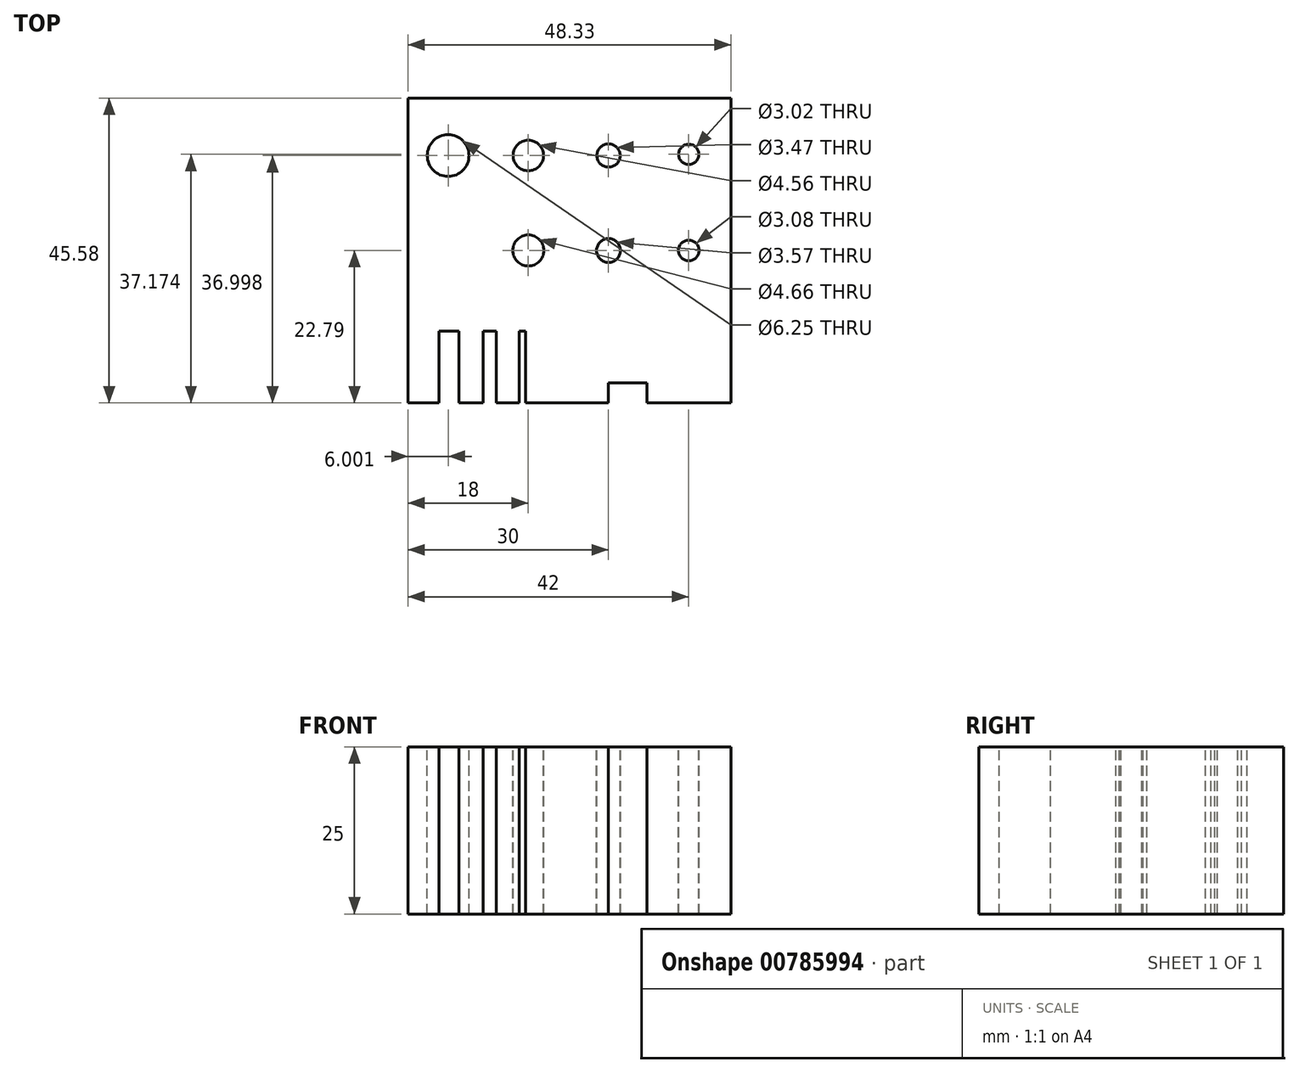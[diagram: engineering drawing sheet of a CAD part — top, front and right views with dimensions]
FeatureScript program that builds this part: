
annotation { "Feature Type Name" : "Feature", "Feature Type Description" : "" }
export const myFeature = defineFeature(function(context is Context, id is Id, definition is map)
    precondition{}
    {
        {
            var Q0;
            Q0=qCreatedBy(makeId("Top.planeOp"),FACE);
            var sketch = newSketch(context, id + "F0", { "sketchPlane" : qUnion([Q0])});
            skLineSegment(sketch, "E0.bottom", {"start": v(30, -22.8) * mm, "end": v(-30, -22.8) * mm});
            skLineSegment(sketch, "E0.top", {"start": v(30, 22.8) * mm, "end": v(-30, 22.8) * mm});
            skLineSegment(sketch, "E0.left", {"start": v(30, -22.8) * mm, "end": v(30, 22.8) * mm});
            skLineSegment(sketch, "E0.right", {"start": v(-30, -22.8) * mm, "end": v(-30, 22.8) * mm});
            skPoint(sketch, "E0.middle", {"position": v(0, 0) * mm});
            skCircle(sketch, "E1", {"center": v(-12, 0) * mm, "radius": 2.33 * mm});
            skCircle(sketch, "E2", {"center": v(0, 0) * mm, "radius": 1.79 * mm});
            skCircle(sketch, "E3", {"center": v(12, 0) * mm, "radius": 1.54 * mm});
            skLineSegment(sketch, "E4", {"start": v(0, 22.8) * mm, "end": v(0, -22.8) * mm, "construction": true});
            skCircle(sketch, "E5", {"center": v(-12, 14.2) * mm, "radius": 2.28 * mm});
            skCircle(sketch, "E6", {"center": v(0, 14.2) * mm, "radius": 1.74 * mm});
            skCircle(sketch, "E7", {"center": v(12, 14.38) * mm, "radius": 1.51 * mm});
            skCircle(sketch, "E8", {"center": v(-24, 14.2) * mm, "radius": 3.12 * mm});
            skLineSegment(sketch, "E9.bottom", {"start": v(0, -22.8) * mm, "end": v(5.74, -22.8) * mm});
            skLineSegment(sketch, "E9.top", {"start": v(0, -19.8) * mm, "end": v(5.74, -19.8) * mm});
            skLineSegment(sketch, "E9.left", {"start": v(0, -22.8) * mm, "end": v(0, -19.8) * mm});
            skLineSegment(sketch, "E9.right", {"start": v(5.74, -22.8) * mm, "end": v(5.74, -19.8) * mm});
            skLineSegment(sketch, "E10.bottom", {"start": v(-13.4, -22.8) * mm, "end": v(-12.4, -22.8) * mm});
            skLineSegment(sketch, "E10.top", {"start": v(-13.4, -12.07) * mm, "end": v(-12.4, -12.07) * mm});
            skLineSegment(sketch, "E10.left", {"start": v(-13.4, -22.8) * mm, "end": v(-13.4, -12.07) * mm});
            skLineSegment(sketch, "E10.right", {"start": v(-12.4, -22.8) * mm, "end": v(-12.4, -12.07) * mm});
            skLineSegment(sketch, "E11.bottom", {"start": v(-25.4, -22.8) * mm, "end": v(-22.4, -22.8) * mm});
            skLineSegment(sketch, "E11.top", {"start": v(-25.4, -12.07) * mm, "end": v(-22.4, -12.07) * mm});
            skLineSegment(sketch, "E11.left", {"start": v(-25.4, -22.8) * mm, "end": v(-25.4, -12.07) * mm});
            skLineSegment(sketch, "E11.right", {"start": v(-22.4, -22.8) * mm, "end": v(-22.4, -12.07) * mm});
            skLineSegment(sketch, "E12.bottom", {"start": v(-18.77, -22.8) * mm, "end": v(-16.77, -22.8) * mm});
            skLineSegment(sketch, "E12.top", {"start": v(-18.77, -12.07) * mm, "end": v(-16.77, -12.07) * mm});
            skLineSegment(sketch, "E12.left", {"start": v(-18.77, -22.8) * mm, "end": v(-18.77, -12.07) * mm});
            skLineSegment(sketch, "E12.right", {"start": v(-16.77, -22.8) * mm, "end": v(-16.77, -12.07) * mm});
            skLineSegment(sketch, "E13", {"start": v(18.33, 22.8) * mm, "end": v(18.33, -22.8) * mm});
            skSolve(sketch);
        }
        {
            var Q0;
            {var subQ14=sQuery(id+"F0.wireOp",EDGE,"E0.right");Q0=makeQuery(id+"F0.imprint","IMPRINT",FACE,{"disambiguationData":[TD([[makeQuery(id+"F0.imprint","IMPRINT",EDGE,{"derivedFrom":subQ14}),-1.0]])]});}
            extrude(context, id + "F1", {"entities" : qUnion([Q0]), "oppositeDirection" : true, "depth" : 25 * mm, "offsetDistance" : 25 * mm});
        }
    });
